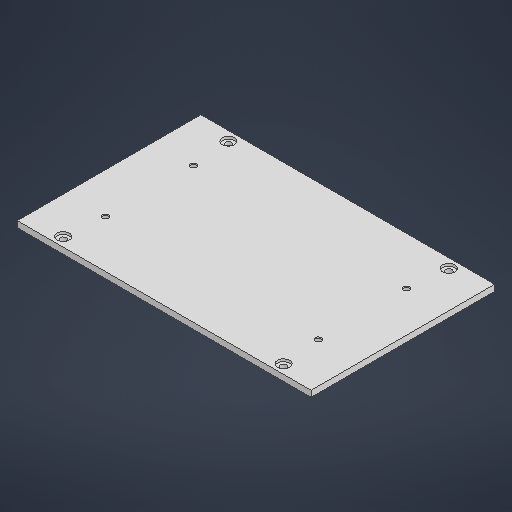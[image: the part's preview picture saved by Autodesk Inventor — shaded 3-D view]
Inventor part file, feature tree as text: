
AUTODESK INVENTOR PART (.ipt)
format: ipt  version: 2025.1 (Build 291241000, 241)  size: 202,752 bytes
history: native  units: mm
features: sketch x3, hole x2, extrude x1, projected_geometry x1
ambient origin geometry x8: Origin, YZ Plane, XZ Plane, XY Plane, X Axis, Y Axis, Z Axis, Center Point
bodies: Solid1 (feature_tree)
feature tree (7):
  extrude  "Extrusion1"  Depth=150.0mm
  hole  "Hole1"  [1 undecoded]
  hole  "Hole2"  [1 undecoded]
  sketch  "Sketch1"  dims[d0=240.0mm d1=150.0mm]
  sketch  "Sketch2"  dims[d2=5.0mm d3=0.0mm d4=72.0mm]
  projected_geometry  "Projected Loop1"
  sketch  "Sketch3"  dims[d5=174.0mm d6=5.0mm d7=6.0mm d8=10.0mm d9=4.0mm d10=90.0deg d11=8.0mm d12=20.594885mm d13=180.0mm d14=135.0mm d15=5.0mm d16=6.0mm d17=10.0mm d18=2.0mm d19=90.0deg d20=3.0mm d21=0.0mm]
note: 2 required parameter values undecoded (feature->parameter linkage not recoverable at this tier; creation-order binding heuristic only, values carry confidence <= 0.55)
